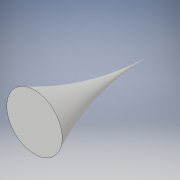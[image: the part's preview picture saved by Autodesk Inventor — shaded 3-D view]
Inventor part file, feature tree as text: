
AUTODESK INVENTOR PART (.ipt)
format: ipt  version: 2017 (Build 210142000, 142)  size: 150,016 bytes
history: native  units: in
note: dims shown in document units (in); Inventor stores cm internally (conversion verified against a paired STEP export)
features: revolve x1, sketch x1
ambient origin geometry x8: Origin, YZ Plane, XZ Plane, XY Plane, X Axis, Y Axis, Z Axis, Center Point
bodies: Solid1 (feature_tree)
feature tree (2):
  revolve  "Revolution1"  [1 undecoded]
  sketch  "Sketch1"  dims[d0=0.75in d1=3.0in d2=90.0deg]
note: 1 required parameter value undecoded (feature->parameter linkage not recoverable at this tier; creation-order binding heuristic only, values carry confidence <= 0.55)
